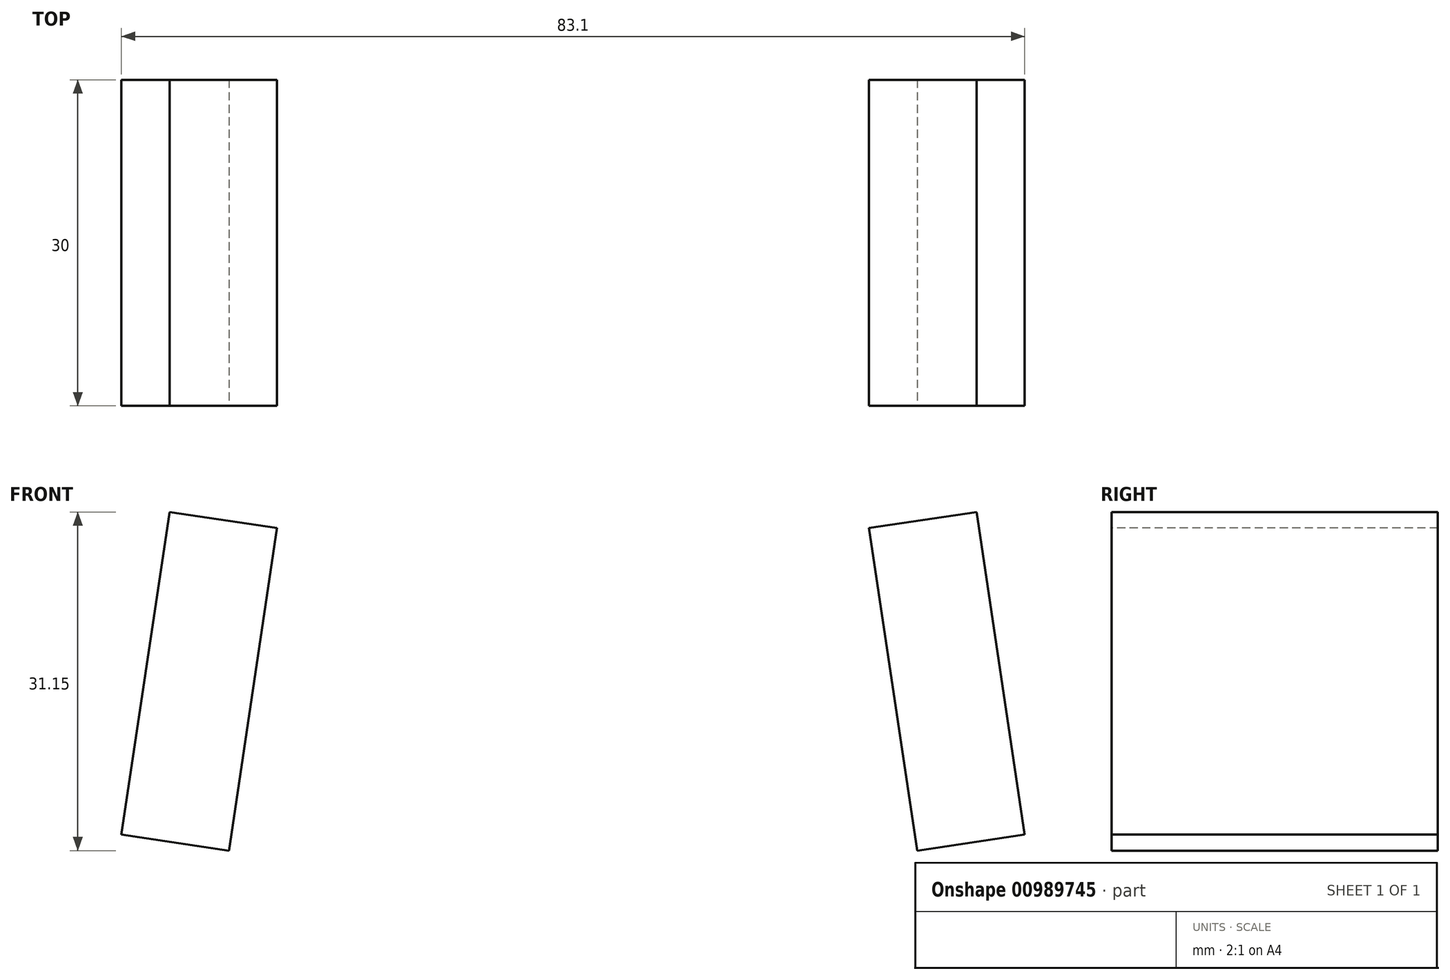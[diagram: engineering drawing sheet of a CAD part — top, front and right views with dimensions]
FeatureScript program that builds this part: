
annotation { "Feature Type Name" : "Feature", "Feature Type Description" : "" }
export const myFeature = defineFeature(function(context is Context, id is Id, definition is map)
    precondition{}
    {
        {
            var Q0;
            Q0=qCreatedBy(makeId("Front.planeOp"),FACE);
            var sketch = newSketch(context, id + "F0", { "sketchPlane" : qUnion([Q0])});
            skLineSegment(sketch, "E0.bottom", {"start": v(-37.12, 34.9) * mm, "end": v(-27.23, 33.42) * mm});
            skLineSegment(sketch, "E0.top", {"start": v(-41.55, 5.23) * mm, "end": v(-31.66, 3.75) * mm});
            skLineSegment(sketch, "E0.left", {"start": v(-37.12, 34.9) * mm, "end": v(-41.55, 5.23) * mm});
            skLineSegment(sketch, "E0.right", {"start": v(-27.23, 33.42) * mm, "end": v(-31.66, 3.75) * mm});
            skLineSegment(sketch, "E1.MirrorCS", {"start": v(37.12, 34.9) * mm, "end": v(27.23, 33.42) * mm});
            skLineSegment(sketch, "E2.MirrorCS", {"start": v(41.55, 5.23) * mm, "end": v(31.66, 3.75) * mm});
            skLineSegment(sketch, "E3.MirrorCS", {"start": v(37.12, 34.9) * mm, "end": v(41.55, 5.23) * mm});
            skLineSegment(sketch, "E4.MirrorCS", {"start": v(27.23, 33.42) * mm, "end": v(31.66, 3.75) * mm});
            skSolve(sketch);
        }
        {
            var Q0;
            Q0=makeQuery(id+"F0.imprint","IMPRINT",FACE,{"disambiguationData":[TD([[makeQuery(id+"F0.imprint","IMPRINT",EDGE,{"derivedFrom":sQuery(id+"F0.wireOp",EDGE,"E1.MirrorCS")}),1.0]])]});
            var Q1;
            Q1=makeQuery(id+"F0.imprint","IMPRINT",FACE,{"disambiguationData":[TD([[makeQuery(id+"F0.imprint","IMPRINT",EDGE,{"derivedFrom":sQuery(id+"F0.wireOp",EDGE,"E0.bottom")}),-1.0]])]});
            extrude(context, id + "F1", {"entities" : qUnion([Q0, Q1]), "oppositeDirection" : true, "depth" : 30 * mm, "offsetDistance" : 25 * mm});
        }
    });
